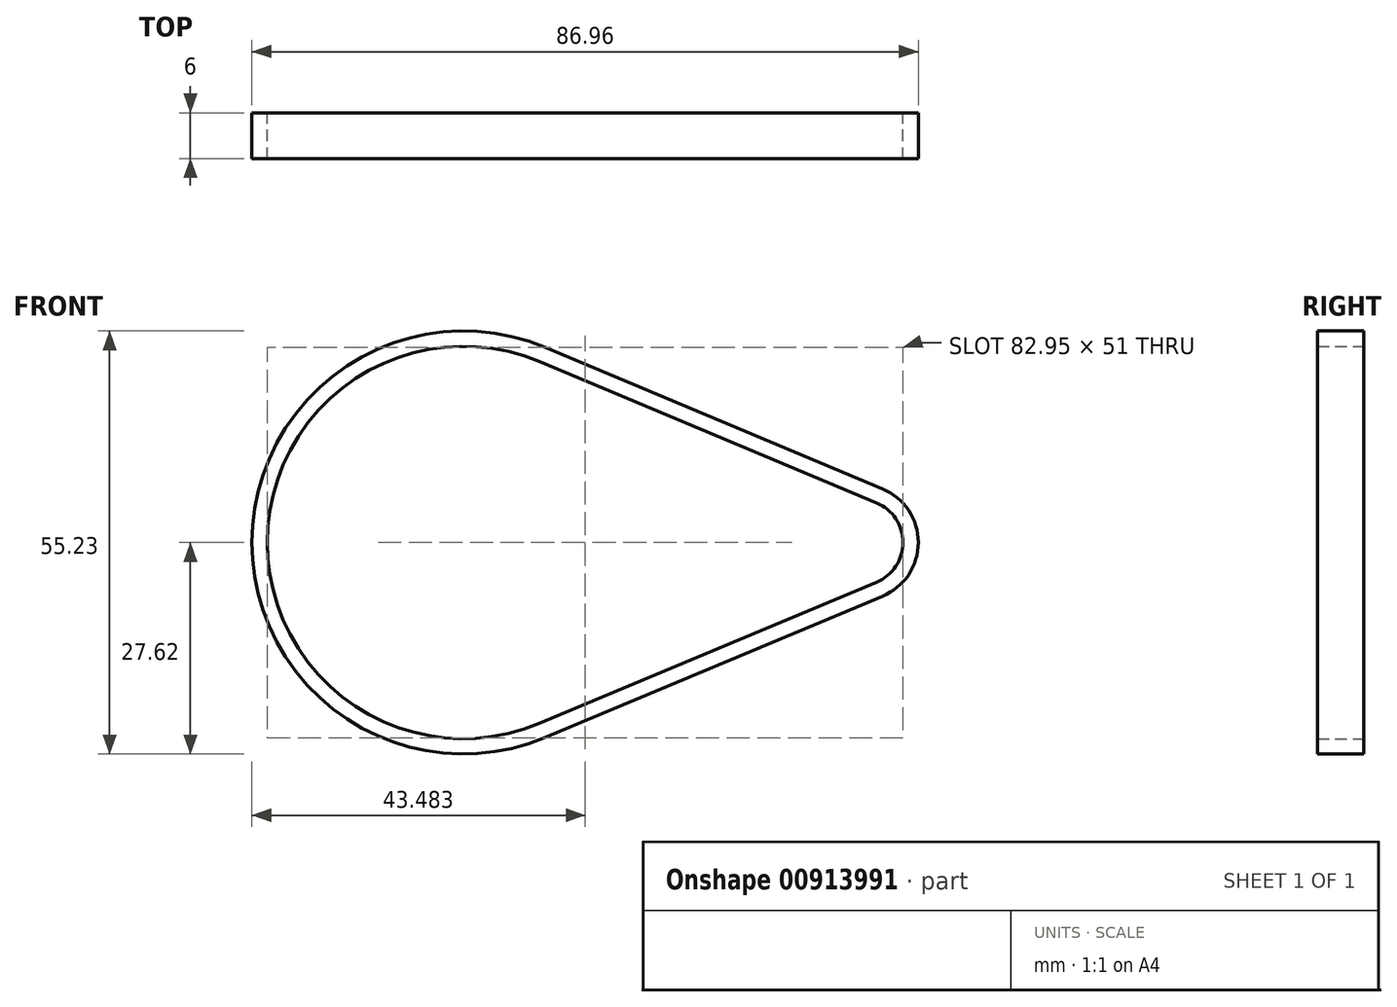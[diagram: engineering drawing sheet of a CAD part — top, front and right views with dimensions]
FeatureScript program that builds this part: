
annotation { "Feature Type Name" : "Feature", "Feature Type Description" : "" }
export const myFeature = defineFeature(function(context is Context, id is Id, definition is map)
    precondition{}
    {
        {
            var Q0;
            Q0=qCreatedBy(makeId("Front.planeOp"),FACE);
            var sketch = newSketch(context, id + "F0", { "sketchPlane" : qUnion([Q0])});
            skCircle(sketch, "E0", {"center": v(0, 0) * mm, "radius": 3 * mm});
            skLineSegment(sketch, "E1", {"start": v(0, 0) * mm, "end": v(-51.74, 0) * mm, "construction": true});
            skCircle(sketch, "E2", {"center": v(-51.74, 0) * mm, "radius": 4 * mm});
            skLineSegment(sketch, "E3", {"start": v(-41.83, 23.62) * mm, "end": v(2.17, 5.16) * mm});
            skLineSegment(sketch, "E4", {"start": v(-41.83, -23.62) * mm, "end": v(2.17, -5.16) * mm});
            skArc(sketch, "E5", {"start": v(-41.83, 23.62) * mm, "mid": v(-77.35, 0) * mm, "end": v(-41.83, -23.62) * mm});
            skArc(sketch, "E6", {"start": v(2.17, 5.16) * mm, "mid": v(5.6, 0) * mm, "end": v(2.17, -5.16) * mm});
            skLineSegment(sketch, "E7", {"start": v(2.17, 5.16) * mm, "end": v(0, 0) * mm, "construction": true});
            skLineSegment(sketch, "E8", {"start": v(2.17, -5.16) * mm, "end": v(0, 0) * mm, "construction": true});
            skArc(sketch, "E9.0", {"start": v(-41.06, 25.47) * mm, "mid": v(-79.36, 0) * mm, "end": v(-41.06, -25.47) * mm});
            skLineSegment(sketch, "E9.1", {"start": v(-41.06, 25.47) * mm, "end": v(2.94, 7) * mm});
            skArc(sketch, "E9.2", {"start": v(2.94, 7) * mm, "mid": v(7.6, 0) * mm, "end": v(2.94, -7) * mm});
            skLineSegment(sketch, "E9.3", {"start": v(-41.06, -25.47) * mm, "end": v(2.94, -7) * mm});
            skSolve(sketch);
        }
        {
            var Q0;
            Q0 = qSketchRegion(id + "F0", true);
            extrude(context, id + "F1", {"entities" : qUnion([Q0]), "depth" : 6 * mm, "offsetDistance" : 25 * mm});
        }
    });
